# Revit family: Pnl_Coating-Doors-ABET-09mm_2250x1000-M3_000000
name_source: partatom
category: Porte
revit_build: Autodesk Revit 2016 (Build: 20150220_1215(x64)
units: mm (PartAtom-declared; Revit-internal decimal feet)

## family parameters
Basato su piano di lavoro = Sì
Condiviso = Sì
Numero OmniClass = 23.30.10.11.27
Punto di calcolo locali = No
Sempre verticale = Sì
Taglio con vuoti quando caricato = Sì
Titolo OmniClass = Door Linings and Boards

## types (1)
- 2250x1000mm
    ABET-Density-ISO_1183 = 1,35 gr/cm3
    ABET-Electrical_R-EN_61340-4-1 = 1x10^9 - 1x10^11 Ohm
    ABET-Flatness-EN_438-2.9 = 60 mm/m
    ABET-Length_Width-EN_438-2.6 = +10/0 mm
    ABET-Lightfastness-EN_438-2.27 = 4 scala grigi (min)
    ABET-R_cigarette_burns-EN_438-2.30 = 3 (min)
    ABET-R_cracking-EN_438-2.24 = 4 (min)
    ABET-R_dry_heat_180dC-App_gloss_fin-EN_438-2.16 = 3 (min)
    ABET-R_dry_heat_180dC-App_other_fin-EN_438-2.16 = 4 (min)
    ABET-R_imm_boiling_water-App_gloss_fin-EN_438-2.12 = 3 (min)
    ABET-R_imm_boiling_water-App_other_fin-EN_438-2.12 = 4 (min)
    ABET-R_impacy_small_D_ball-Spring_F-EN_438-2.20 = 20 N (min)
    ABET-R_scratching-EN_438-2.25 = 3 (min)
    ABET-R_scrubbing-HGS_gloss_fin-LM_086 = 200 n.cicli
    ABET-R_scrubbing-HR-LAQ_gloss_fin-LM_086 = 2000 n.cicli
    ABET-R_staining-App_group_3-EN_438-2.26 = 4 (min)
    ABET-R_staining-App_groups_1_2-EN_438-2.26 = 5 (min)
    ABET-R_surface_wear-Inial_point-EN_438-2.10 = 150 giri (min)
    ABET-R_surface_wear-Wear_value-EN_438-2.10 = 350 giri (min)
    ABET-R_water_vapour-App_gloss_fin-EN_438-2.14 = 3 (min)
    ABET-R_water_vapour-App_other_fin-EN_438-2.14 = 4 (min)
    ABET-R_wet_heat_100dC-App_gloss_fin-EN_12721 = 4 (min)
    ABET-R_wet_heat_100dC-App_other_fin-EN_12721 = 3 (min)
    ABET-Squareness-EN_438-2.8 = 1,5 mm/m
    ABET-Stability_elevated_Temp-L-EN_438-2.17 = 0,55% max
    ABET-Stability_elevated_Temp-T-EN_438-2.17 = 1,05% max
    ABET-Straightness_edges-EN_438-2.7 = 1,5 mm/m
    ABET-Thickness-EN_438-2.5 = ± 0,10 mm
    ABET_Length = 2250 mm
    ABET_Length_max = 2250 mm
    ABET_Length_value = 2250 mm
    ABET_Thickness = 0.9 mm  [stored 0.00295276 ft]
    ABET_Width = 1000 mm  [stored 3.28084 ft]
    ABET_Width_max = 1000 mm  [stored 3.28084 ft]
    ABET_Width_value = 1000 mm  [stored 3.28084 ft]
    COBie_Cost = 0
    COBie_ExpectedLife = 0
    COBie_ReplacementCost = 0
    COBie_WarrantyDurationLabour = 0
    COBie_WarrantyDurationParts = 0
    Commenti sul tipo = 0.9mm_2250x1000mm
    IfcExportAs = IfcDoor
    IfcExportType = NOTDEFINED
    Modello = Doors
    Produttore = Abet Laminati S.P.A.
    Prospetto di default = 0 mm  [stored 0 ft]
    Sys_URL(ManufacturerWebsite) = http://abetlaminati.com
    Sys_URL(TechnicalProductDataSheet) = http://abetlaminati.com
    Sys_URL(Use-and-MaintenanceManual) = http://abetlaminati.com
    URL = http://abetlaminati.com
    Uniclass2015_Code = Pr_25_71_63_15
    Uniclass_2015_Description = Compact or solid grade high-pressure laminate (HPL) boards

note: [stored X ft] marks values corroborated as IEEE doubles in the binary element streams (Revit-internal decimal feet)

## geometry (parser evidence)
native form markers: Sweep x3
no freeform markers — native parametric forms only
